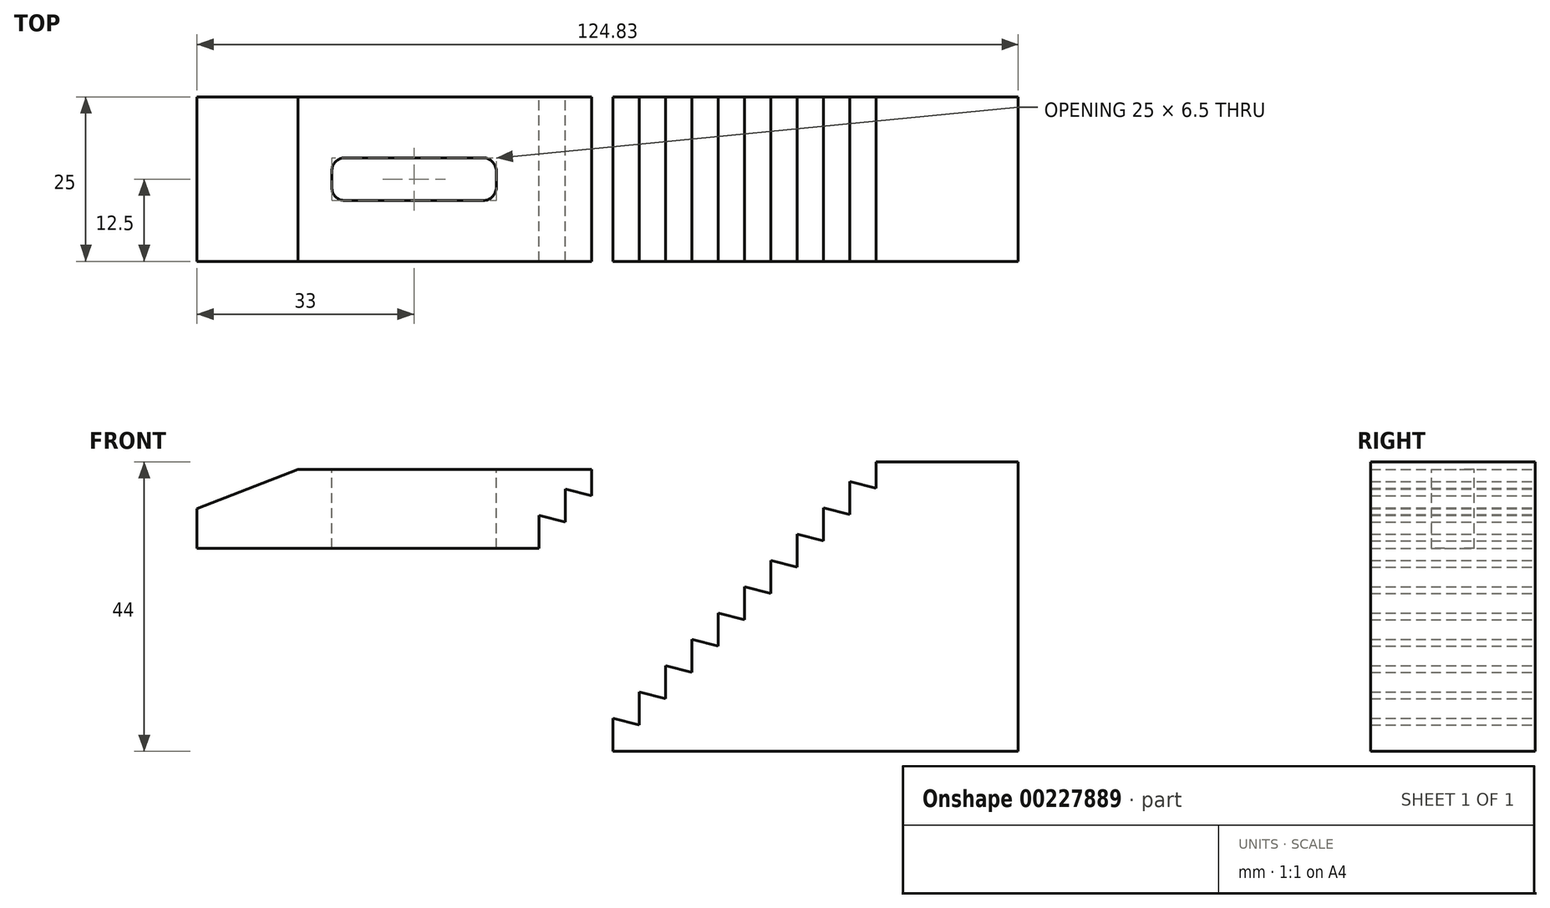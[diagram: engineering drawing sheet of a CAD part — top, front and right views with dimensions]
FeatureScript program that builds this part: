
annotation { "Feature Type Name" : "Feature", "Feature Type Description" : "" }
export const myFeature = defineFeature(function(context is Context, id is Id, definition is map)
    precondition{}
    {
        {
            var Q0;
            Q0=qCreatedBy(makeId("Front.planeOp"),FACE);
            var sketch = newSketch(context, id + "F0", { "sketchPlane" : qUnion([Q0])});
            skLineSegment(sketch, "E0.bottom", {"start": v(-36.67, 20.59) * mm, "end": v(8, 20.59) * mm});
            skLineSegment(sketch, "E0.top", {"start": v(-52, 8.59) * mm, "end": v(0, 8.59) * mm});
            skLineSegment(sketch, "E0.left", {"start": v(-52, 14.59) * mm, "end": v(-52, 8.59) * mm});
            skLineSegment(sketch, "E1.trimOffspring", {"start": v(4, 12.59) * mm, "end": v(0, 13.59) * mm});
            skLineSegment(sketch, "E2.trimOffspring", {"start": v(4, 17.59) * mm, "end": v(4, 12.59) * mm});
            skLineSegment(sketch, "E3.trimOffspring", {"start": v(0, 13.59) * mm, "end": v(0, 8.59) * mm});
            skPoint(sketch, "E4.start.orphan", {"position": v(0, 21.54) * mm});
            skLineSegment(sketch, "E5", {"start": v(8, 20.59) * mm, "end": v(8, 16.59) * mm});
            skLineSegment(sketch, "E6", {"start": v(8, 16.59) * mm, "end": v(4, 17.59) * mm});
            skLineSegment(sketch, "E7.trimOffspring", {"start": v(47.25, 13.72) * mm, "end": v(43.25, 14.72) * mm});
            skLineSegment(sketch, "E8.trimOffspring", {"start": v(47.25, 18.72) * mm, "end": v(47.25, 13.72) * mm});
            skLineSegment(sketch, "E9.trimOffspring", {"start": v(43.25, 14.72) * mm, "end": v(43.25, 9.72) * mm});
            skLineSegment(sketch, "E10", {"start": v(51.25, 21.72) * mm, "end": v(51.25, 17.72) * mm});
            skLineSegment(sketch, "E11", {"start": v(51.25, 17.72) * mm, "end": v(47.25, 18.72) * mm});
            skLineSegment(sketch, "E12.trimOffspring", {"start": v(39.25, 5.72) * mm, "end": v(35.25, 6.72) * mm});
            skLineSegment(sketch, "E13.trimOffspring", {"start": v(39.25, 10.72) * mm, "end": v(39.25, 5.72) * mm});
            skLineSegment(sketch, "E14.trimOffspring", {"start": v(35.25, 6.72) * mm, "end": v(35.25, 1.72) * mm});
            skLineSegment(sketch, "E15", {"start": v(43.25, 9.72) * mm, "end": v(39.25, 10.72) * mm});
            skLineSegment(sketch, "E16.trimOffspring", {"start": v(31.25, -2.28) * mm, "end": v(27.25, -1.28) * mm});
            skLineSegment(sketch, "E17.trimOffspring", {"start": v(31.25, 2.72) * mm, "end": v(31.25, -2.28) * mm});
            skLineSegment(sketch, "E18.trimOffspring", {"start": v(27.25, -1.28) * mm, "end": v(27.25, -6.28) * mm});
            skLineSegment(sketch, "E19", {"start": v(35.25, 1.72) * mm, "end": v(31.25, 2.72) * mm});
            skLineSegment(sketch, "E20", {"start": v(51.25, 21.72) * mm, "end": v(72.83, 21.72) * mm});
            skLineSegment(sketch, "E21", {"start": v(72.83, 21.72) * mm, "end": v(72.83, -22.28) * mm});
            skLineSegment(sketch, "E22", {"start": v(72.83, -22.28) * mm, "end": v(11.1, -22.28) * mm});
            skLineSegment(sketch, "E23.trimOffspring", {"start": v(23.25, -10.28) * mm, "end": v(19.25, -9.28) * mm});
            skLineSegment(sketch, "E24.trimOffspring", {"start": v(23.25, -5.28) * mm, "end": v(23.25, -10.28) * mm});
            skLineSegment(sketch, "E25.trimOffspring", {"start": v(19.25, -9.28) * mm, "end": v(19.25, -14.28) * mm});
            skLineSegment(sketch, "E26", {"start": v(27.25, -6.28) * mm, "end": v(23.25, -5.28) * mm});
            skLineSegment(sketch, "E27.trimOffspring", {"start": v(15.25, -18.28) * mm, "end": v(11.25, -17.28) * mm});
            skLineSegment(sketch, "E28.trimOffspring", {"start": v(15.25, -13.28) * mm, "end": v(15.25, -18.28) * mm});
            skLineSegment(sketch, "E29.trimOffspring", {"start": v(11.25, -17.28) * mm, "end": v(11.25, -22.28) * mm});
            skLineSegment(sketch, "E30", {"start": v(19.25, -14.28) * mm, "end": v(15.25, -13.28) * mm});
            skLineSegment(sketch, "E31", {"start": v(-52, 14.59) * mm, "end": v(-36.67, 20.59) * mm});
            skPoint(sketch, "E32.orphan", {"position": v(-52, 20.59) * mm});
            skSolve(sketch);
        }
        {
            var Q0;
            Q0=makeQuery(id+"F0.imprint","IMPRINT",FACE,{"disambiguationData":[TD([[makeQuery(id+"F0.imprint","IMPRINT",EDGE,{"derivedFrom":sQuery(id+"F0.wireOp",EDGE,"E0.bottom")}),-1.0]])]});
            var Q1;
            Q1=makeQuery(id+"F0.imprint","IMPRINT",FACE,{"disambiguationData":[TD([[makeQuery(id+"F0.imprint","IMPRINT",EDGE,{"derivedFrom":sQuery(id+"F0.wireOp",EDGE,"E7.trimOffspring")}),1.0]])]});
            extrude(context, id + "F1", {"entities" : qUnion([Q0, Q1]), "depth" : 25 * mm});
        }
        {
            var Q0;
            Q0=makeQuery(id+"F1.opExtrude","SWEPT_FACE",FACE,{"disambiguationData":[OSD([sQuery(id+"F0.wireOp",EDGE,"E0.bottom")])]});
            var sketch = newSketch(context, id + "F2", { "sketchPlane" : qUnion([Q0])});
            skLineSegment(sketch, "E33.bottom", {"start": v(-29.5, -15.75) * mm, "end": v(-8.5, -15.75) * mm});
            skLineSegment(sketch, "E33.top", {"start": v(-29.5, -9.25) * mm, "end": v(-8.5, -9.25) * mm});
            skLineSegment(sketch, "E33.left", {"start": v(-31.5, -13.75) * mm, "end": v(-31.5, -11.25) * mm});
            skLineSegment(sketch, "E33.right", {"start": v(-6.5, -13.75) * mm, "end": v(-6.5, -11.25) * mm});
            skPoint(sketch, "E34.visualSharp", {"position": v(-31.5, -15.75) * mm});
            skArc(sketch, "E34.filletArc", {"start": v(-31.5, -13.75) * mm, "mid": v(-30.91, -15.16) * mm, "end": v(-29.5, -15.75) * mm});
            skPoint(sketch, "E35.visualSharp", {"position": v(-31.5, -9.25) * mm});
            skArc(sketch, "E35.filletArc", {"start": v(-29.5, -9.25) * mm, "mid": v(-30.91, -9.84) * mm, "end": v(-31.5, -11.25) * mm});
            skPoint(sketch, "E36.visualSharp", {"position": v(-6.5, -9.25) * mm});
            skArc(sketch, "E36.filletArc", {"start": v(-6.5, -11.25) * mm, "mid": v(-7.09, -9.84) * mm, "end": v(-8.5, -9.25) * mm});
            skPoint(sketch, "E37.visualSharp", {"position": v(-6.5, -15.75) * mm});
            skArc(sketch, "E37.filletArc", {"start": v(-8.5, -15.75) * mm, "mid": v(-7.09, -15.16) * mm, "end": v(-6.5, -13.75) * mm});
            skSolve(sketch);
        }
        {
            var Q0;
            Q0 = qSketchRegion(id + "F2", true);
            extrude(context, id + "F3", {"entities" : qUnion([Q0]), "operationType" : NewBodyOperationType.REMOVE, "oppositeDirection" : true, "depth" : 25 * mm});
        }
    });
